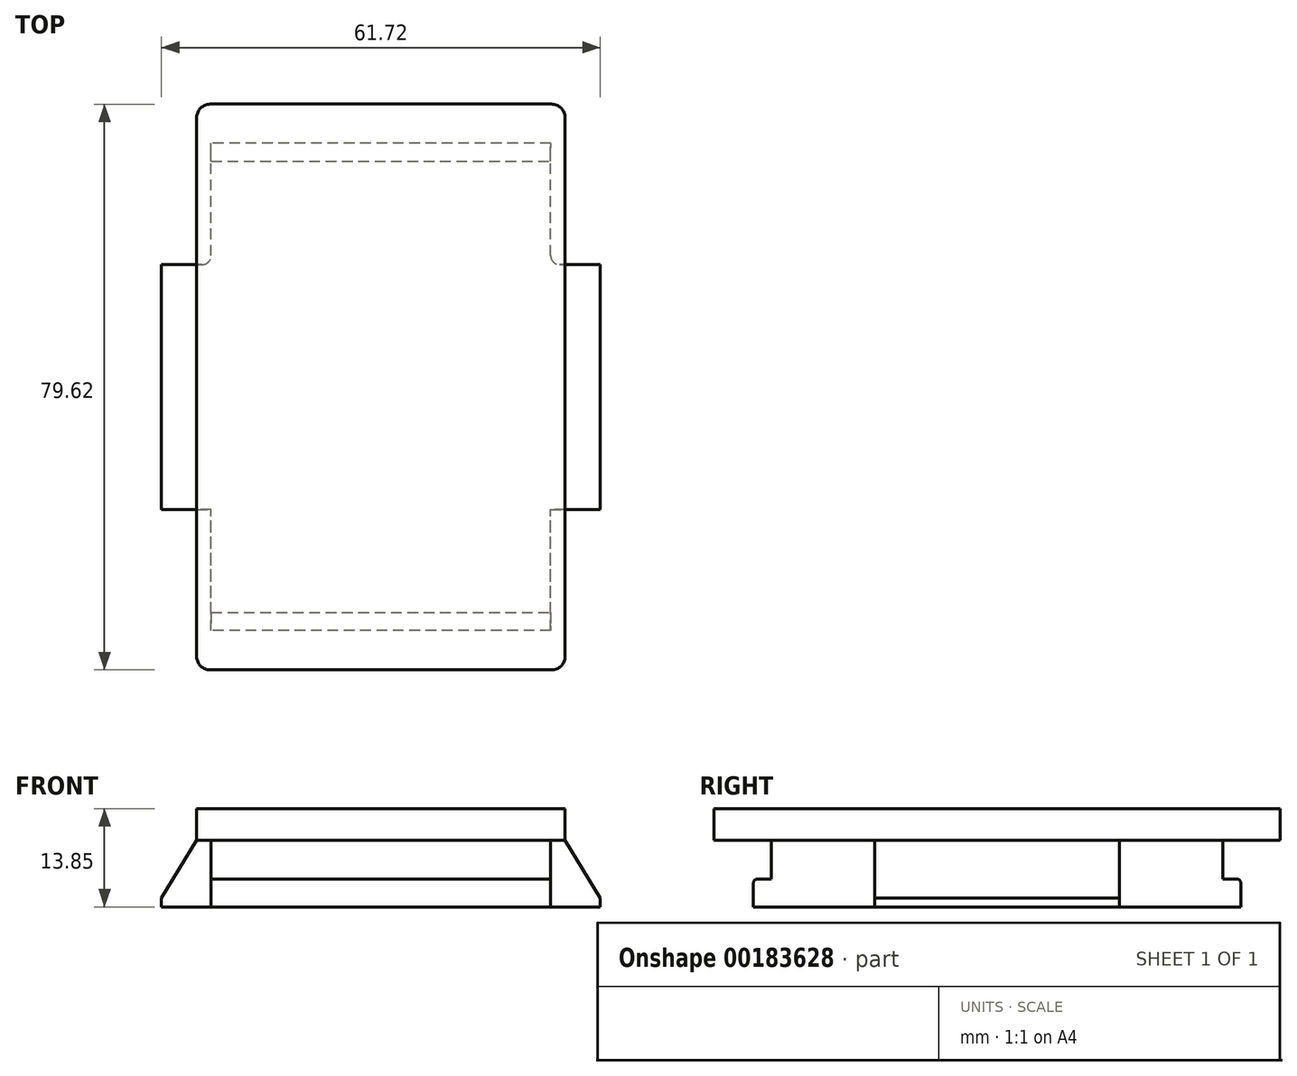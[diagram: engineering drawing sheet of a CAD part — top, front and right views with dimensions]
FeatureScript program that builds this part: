
annotation { "Feature Type Name" : "Feature", "Feature Type Description" : "" }
export const myFeature = defineFeature(function(context is Context, id is Id, definition is map)
    precondition{}
    {
        {
            var Q0;
            Q0=qCreatedBy(makeId("Top.planeOp"),FACE);
            var sketch = newSketch(context, id + "F0", { "sketchPlane" : qUnion([Q0])});
            skLineSegment(sketch, "E0.bottom", {"start": v(24, -39.81) * mm, "end": v(-24, -39.81) * mm});
            skLineSegment(sketch, "E0.top", {"start": v(24, 39.81) * mm, "end": v(-24, 39.81) * mm});
            skLineSegment(sketch, "E0.left", {"start": v(25.9, -37.9) * mm, "end": v(25.9, 37.9) * mm});
            skLineSegment(sketch, "E0.right", {"start": v(-25.9, -37.9) * mm, "end": v(-25.9, 37.9) * mm});
            skPoint(sketch, "E0.middle", {"position": v(0, 0) * mm});
            skPoint(sketch, "E1.visualSharp", {"position": v(-25.9, 39.81) * mm});
            skArc(sketch, "E1.filletArc", {"start": v(-24, 39.81) * mm, "mid": v(-25.35, 39.26) * mm, "end": v(-25.9, 37.9) * mm});
            skPoint(sketch, "E2.visualSharp", {"position": v(25.9, 39.81) * mm});
            skArc(sketch, "E2.filletArc", {"start": v(25.9, 37.9) * mm, "mid": v(25.35, 39.26) * mm, "end": v(24, 39.81) * mm});
            skPoint(sketch, "E3.visualSharp", {"position": v(-25.9, -39.81) * mm});
            skArc(sketch, "E3.filletArc", {"start": v(-25.9, -37.9) * mm, "mid": v(-25.35, -39.26) * mm, "end": v(-24, -39.81) * mm});
            skPoint(sketch, "E4.visualSharp", {"position": v(25.9, -39.81) * mm});
            skArc(sketch, "E4.filletArc", {"start": v(24, -39.81) * mm, "mid": v(25.35, -39.26) * mm, "end": v(25.9, -37.9) * mm});
            skSolve(sketch);
        }
        {
            var Q0;
            Q0 = qSketchRegion(id + "F0", true);
            extrude(context, id + "F1", {"entities" : qUnion([Q0]), "depth" : 4.44 * mm});
        }
        {
            var Q0;
            Q0=makeQuery(id+"F1.opExtrude","CAP_FACE",FACE,{"disambiguationData":[OSD([sQuery(id+"F0.wireOp",EDGE,"E0.bottom"),sQuery(id+"F0.wireOp",EDGE,"E0.top"),sQuery(id+"F0.wireOp",EDGE,"E0.left"),sQuery(id+"F0.wireOp",EDGE,"E0.right"),sQuery(id+"F0.wireOp",EDGE,"E1.filletArc"),sQuery(id+"F0.wireOp",EDGE,"E2.filletArc"),sQuery(id+"F0.wireOp",EDGE,"E3.filletArc"),sQuery(id+"F0.wireOp",EDGE,"E4.filletArc")])],"isStart":true});
            var sketch = newSketch(context, id + "F2", { "sketchPlane" : qUnion([Q0])});
            skLineSegment(sketch, "E5.bottom", {"start": v(-23.88, 31.75) * mm, "end": v(23.88, 31.75) * mm});
            skLineSegment(sketch, "E5.top", {"start": v(-23.88, -31.75) * mm, "end": v(23.88, -31.75) * mm});
            skLineSegment(sketch, "E5.left", {"start": v(-23.88, 31.75) * mm, "end": v(-23.88, -31.75) * mm});
            skLineSegment(sketch, "E5.right", {"start": v(23.88, 31.75) * mm, "end": v(23.88, -31.75) * mm});
            skPoint(sketch, "E5.middle", {"position": v(0, 0) * mm});
            skSolve(sketch);
        }
        {
            var Q0;
            Q0 = qSketchRegion(id + "F2", true);
            extrude(context, id + "F3", {"entities" : qUnion([Q0]), "operationType" : NewBodyOperationType.ADD, "depth" : 9.4 * mm});
        }
        {
            var Q0;
            Q0=makeQuery(id+"F3.opExtrude","SWEPT_FACE",FACE,{"disambiguationData":[OSD([sQuery(id+"F2.wireOp",EDGE,"E5.left")])]});
            var sketch = newSketch(context, id + "F4", { "sketchPlane" : qUnion([Q0])});
            skLineSegment(sketch, "E6.bottom", {"start": v(-31.75, -9.4) * mm, "end": v(-34.3, -9.4) * mm});
            skLineSegment(sketch, "E6.top", {"start": v(-31.75, -5.46) * mm, "end": v(-33.66, -5.46) * mm});
            skLineSegment(sketch, "E6.left", {"start": v(-31.75, -9.4) * mm, "end": v(-31.75, -5.46) * mm});
            skLineSegment(sketch, "E6.right", {"start": v(-34.3, -9.4) * mm, "end": v(-34.3, -6.1) * mm});
            skPoint(sketch, "E7.visualSharp", {"position": v(-34.3, -5.46) * mm});
            skArc(sketch, "E7.filletArc", {"start": v(-33.66, -5.46) * mm, "mid": v(-34.1, -5.65) * mm, "end": v(-34.3, -6.1) * mm});
            skArc(sketch, "E8.MirrorCS", {"start": v(33.65, -5.46) * mm, "mid": v(34.1, -5.65) * mm, "end": v(34.3, -6.1) * mm});
            skLineSegment(sketch, "E9.MirrorCS", {"start": v(31.75, -9.4) * mm, "end": v(31.75, -5.46) * mm});
            skLineSegment(sketch, "E10.MirrorCS", {"start": v(31.75, -5.46) * mm, "end": v(33.65, -5.46) * mm});
            skLineSegment(sketch, "E11.MirrorCS", {"start": v(31.75, -9.4) * mm, "end": v(34.3, -9.4) * mm});
            skLineSegment(sketch, "E12.MirrorCS", {"start": v(34.3, -9.4) * mm, "end": v(34.3, -6.1) * mm});
            skSolve(sketch);
        }
        {
            var Q0;
            Q0 = qSketchRegion(id + "F4", true);
            var Q1;
            Q1=makeQuery(id+"F3.opExtrude","SWEPT_FACE",FACE,{"disambiguationData":[OSD([sQuery(id+"F2.wireOp",EDGE,"E5.right")])]});
            extrude(context, id + "F5", {"entities" : qUnion([Q0]), "operationType" : NewBodyOperationType.ADD, "endBound" : BoundingType.UP_TO_SURFACE, "oppositeDirection" : true, "endBoundEntityFace" : qUnion([Q1]), "depth" : 25.4 * mm});
        }
        {
            var Q0;
            Q0=qCreatedBy(makeId("Front.planeOp"),FACE);
            var sketch = newSketch(context, id + "F6", { "sketchPlane" : qUnion([Q0])});
            skLineSegment(sketch, "E13", {"start": v(-23.88, -9.4) * mm, "end": v(-30.86, -9.4) * mm});
            skLineSegment(sketch, "E14", {"start": v(-30.86, -9.4) * mm, "end": v(-30.86, -8.13) * mm});
            skLineSegment(sketch, "E15", {"start": v(-30.86, -8.13) * mm, "end": v(-25.9, 0) * mm});
            skLineSegment(sketch, "E16", {"start": v(-25.9, 0) * mm, "end": v(-23.88, 0) * mm});
            skLineSegment(sketch, "E17", {"start": v(-23.88, 0) * mm, "end": v(-23.88, -9.4) * mm});
            skLineSegment(sketch, "E18.MirrorCS", {"start": v(30.86, -8.13) * mm, "end": v(25.9, 0) * mm});
            skLineSegment(sketch, "E19.MirrorCS", {"start": v(30.86, -9.4) * mm, "end": v(30.86, -8.13) * mm});
            skLineSegment(sketch, "E20.MirrorCS", {"start": v(23.88, -9.4) * mm, "end": v(30.86, -9.4) * mm});
            skLineSegment(sketch, "E21.MirrorCS", {"start": v(25.9, 0) * mm, "end": v(23.88, 0) * mm});
            skLineSegment(sketch, "E22.MirrorCS", {"start": v(23.88, 0) * mm, "end": v(23.88, -9.4) * mm});
            skSolve(sketch);
        }
        {
            var Q0;
            Q0 = qSketchRegion(id + "F6", true);
            extrude(context, id + "F7", {"entities" : qUnion([Q0]), "operationType" : NewBodyOperationType.ADD, "depth" : 17.22 * mm, "hasSecondDirection" : true, "secondDirectionOppositeDirection" : true, "secondDirectionDepth" : 17.22 * mm});
        }
        {
            var Q0;
            Q0=makeQuery(id+"F7.opExtrude","CAP_EDGE",EDGE,{"disambiguationData":[OSD([sQuery(id+"F6.wireOp",EDGE,"E22.MirrorCS")])],"isStart":false});
            var Q1;
            Q1=makeQuery(id+"F7.opExtrude","CAP_EDGE",EDGE,{"disambiguationData":[OSD([sQuery(id+"F6.wireOp",EDGE,"E22.MirrorCS")])],"isStart":true});
            var Q2;
            Q2=makeQuery(id+"F7.opExtrude","CAP_EDGE",EDGE,{"disambiguationData":[OSD([sQuery(id+"F6.wireOp",EDGE,"E17")])],"isStart":true});
            var Q3;
            Q3=makeQuery(id+"F7.opExtrude","CAP_EDGE",EDGE,{"disambiguationData":[OSD([sQuery(id+"F6.wireOp",EDGE,"E17")])],"isStart":false});
            fillet(context, id + "F8", {"entities" : qUnion([Q0, Q1, Q2, Q3]), "radius" : 1.27 * mm, "tangentPropagation" : true, "allowEdgeOverflow" : false});
        }
    });
